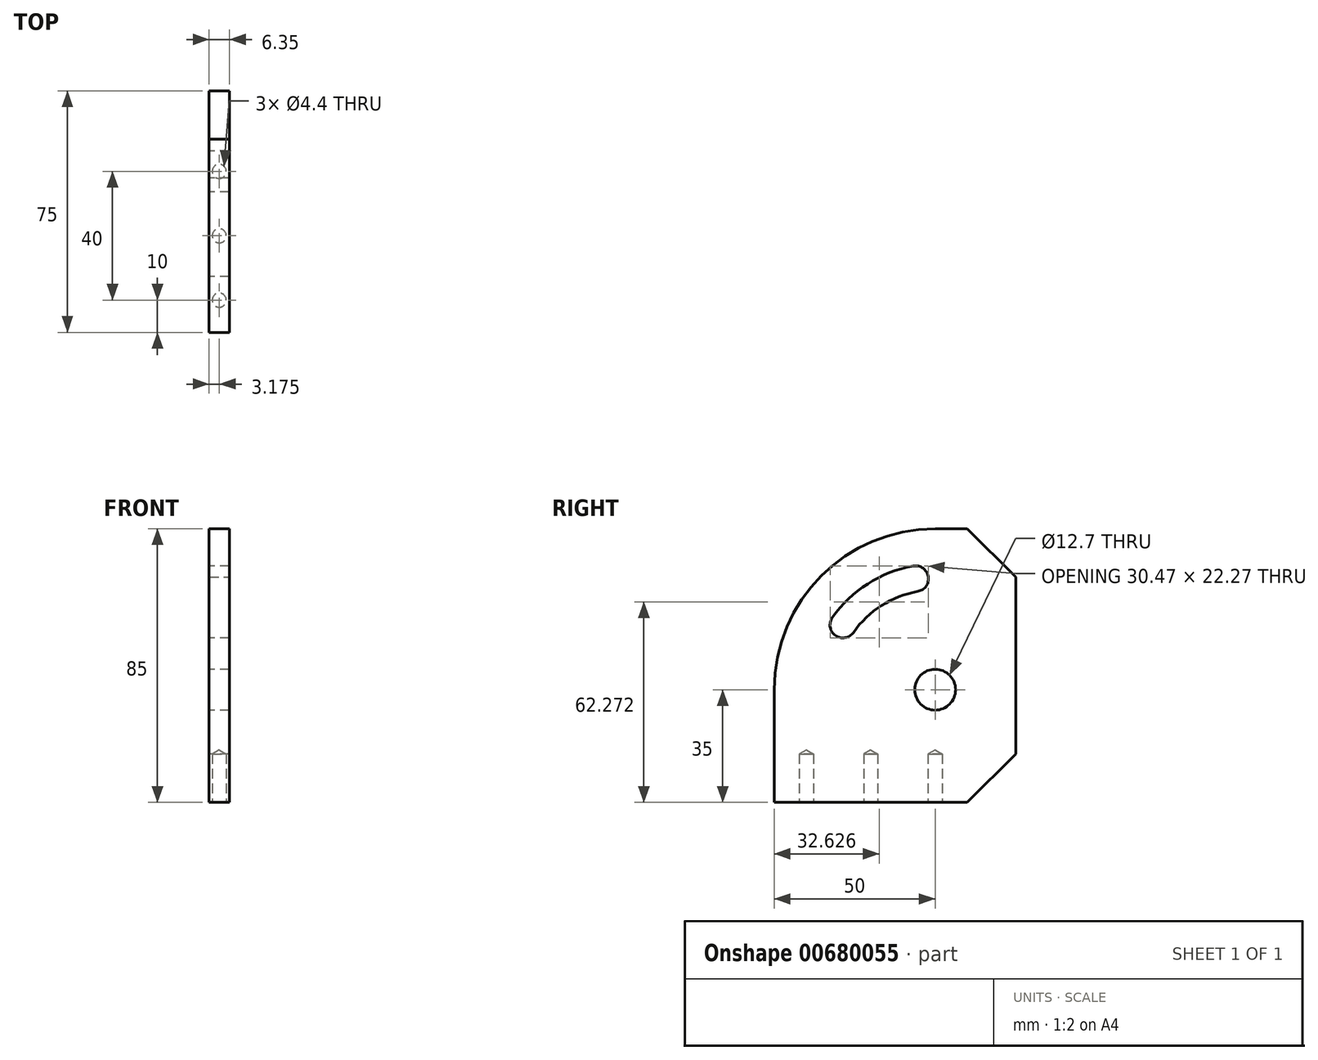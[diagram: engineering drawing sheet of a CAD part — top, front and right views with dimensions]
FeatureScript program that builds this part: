
annotation { "Feature Type Name" : "Feature", "Feature Type Description" : "" }
export const myFeature = defineFeature(function(context is Context, id is Id, definition is map)
    precondition{}
    {
        {
            var Q0;
            Q0=qCreatedBy(makeId("Right.planeOp"),FACE);
            var sketch = newSketch(context, id + "F0", { "sketchPlane" : qUnion([Q0])});
            skLineSegment(sketch, "E0", {"start": v(0, 0) * mm, "end": v(-75, 0) * mm});
            skLineSegment(sketch, "E1", {"start": v(-75, 0) * mm, "end": v(-75, 35) * mm});
            skArc(sketch, "E2", {"start": v(-25, 85) * mm, "mid": v(-60.36, 70.36) * mm, "end": v(-75, 35) * mm});
            skLineSegment(sketch, "E3", {"start": v(-25, 85) * mm, "end": v(0, 85) * mm});
            skLineSegment(sketch, "E4", {"start": v(0, 85) * mm, "end": v(0, 0) * mm});
            skArc(sketch, "E5", {"start": v(-56.95, 57.37) * mm, "mid": v(-45.95, 67.9) * mm, "end": v(-31.77, 73.4) * mm});
            skArc(sketch, "E6.0", {"start": v(-53.67, 55.08) * mm, "mid": v(-43.8, 64.52) * mm, "end": v(-31.08, 69.47) * mm, "construction": true});
            skArc(sketch, "E7.0", {"start": v(-50.4, 52.78) * mm, "mid": v(-41.66, 61.15) * mm, "end": v(-30.38, 65.53) * mm});
            skArc(sketch, "E8", {"start": v(-31.77, 73.4) * mm, "mid": v(-27.14, 70.16) * mm, "end": v(-30.38, 65.53) * mm});
            skArc(sketch, "E9", {"start": v(-56.95, 57.37) * mm, "mid": v(-55.96, 51.8) * mm, "end": v(-50.4, 52.78) * mm});
            skCircle(sketch, "E10", {"center": v(-25, 35) * mm, "radius": 6.35 * mm});
            skLineSegment(sketch, "E11", {"start": v(-31.08, 69.47) * mm, "end": v(-25, 35) * mm, "construction": true});
            skLineSegment(sketch, "E12", {"start": v(-53.67, 55.08) * mm, "end": v(-25, 35) * mm, "construction": true});
            skSolve(sketch);
        }
        {
            var Q0;
            Q0 = qSketchRegion(id + "F0", true);
            extrude(context, id + "F1", {"entities" : qUnion([Q0]), "depth" : 6.35 * mm, "offsetDistance" : 25 * mm});
        }
        {
            var Q0;
            Q0=makeQuery(id+"F1.opExtrude","SWEPT_EDGE",EDGE,{"disambiguationData":[OSD([sQuery(id+"F0.wireOp",EDGE,"E3"),sQuery(id+"F0.wireOp",EDGE,"E4")])]});
            var Q1;
            Q1=makeQuery(id+"F1.opExtrude","SWEPT_EDGE",EDGE,{"disambiguationData":[OSD([sQuery(id+"F0.wireOp",EDGE,"E0"),sQuery(id+"F0.wireOp",EDGE,"E4")])]});
            chamfer(context, id + "F2", {"entities" : qUnion([Q0, Q1]), "width" : 15 * mm, "tangentPropagation" : true});
        }
        {
            var Q0;
            Q0=makeQuery(id+"F1.opExtrude","SWEPT_FACE",FACE,{"disambiguationData":[OSD([sQuery(id+"F0.wireOp",EDGE,"E0")])]});
            var sketch = newSketch(context, id + "F3", { "sketchPlane" : qUnion([Q0])});
            skPoint(sketch, "E13", {"position": v(3.18, 65) * mm});
            skPoint(sketch, "E14", {"position": v(3.18, 45) * mm});
            skPoint(sketch, "E15", {"position": v(3.18, 25) * mm});
            skLineSegment(sketch, "E16", {"start": v(3.18, 65) * mm, "end": v(3.18, 45) * mm, "construction": true});
            skLineSegment(sketch, "E17", {"start": v(3.18, 25) * mm, "end": v(3.18, 45) * mm, "construction": true});
            skLineSegment(sketch, "E18", {"start": v(3.18, 65) * mm, "end": v(3.18, 75) * mm, "construction": true});
            skSolve(sketch);
        }
        {
            var Q0;
            Q0=sQuery(id+"F3.wireOp",VERTEX,"E13");
            var Q1;
            Q1=sQuery(id+"F3.wireOp",VERTEX,"E14");
            var Q2;
            Q2=sQuery(id+"F3.wireOp",VERTEX,"E15");
            var Q3;
            Q3=makeQuery(id+"F1.opExtrude","SWEPT_BODY",BODY,{"disambiguationData":[OSD([sQuery(id+"F0.wireOp",EDGE,"E0"),sQuery(id+"F0.wireOp",EDGE,"E1"),sQuery(id+"F0.wireOp",EDGE,"E2"),sQuery(id+"F0.wireOp",EDGE,"E3"),sQuery(id+"F0.wireOp",EDGE,"E4"),sQuery(id+"F0.wireOp",EDGE,"E5"),sQuery(id+"F0.wireOp",EDGE,"E7.0"),sQuery(id+"F0.wireOp",EDGE,"E8"),sQuery(id+"F0.wireOp",EDGE,"E9"),sQuery(id+"F0.wireOp",EDGE,"E10")])]});
            hole(context, id + "F4", {"style" : HoleStyle.SIMPLE, "endStyle" : HoleEndStyle.BLIND, "standardTappedOrClearance" : lookupTablePath({ "standard" : "ISO", "fit" : "Normal", "size" : "M4", "type" : "Clearance" }), "standardBlindInLast" : lookupTablePath({ "fit" : "Standard", "standard" : "ISO", "size" : "M4", "type" : "Clearance" }), "holeDiameter" : 4.4 * mm, "majorDiameter" : 5 * mm, "holeDepth" : 15 * mm, "isTappedThrough" : true, "tappedDepth" : 12 * mm, "tapClearance" : 3, "locations" : qUnion([Q0, Q1, Q2]), "scope" : qUnion([Q3])});
        }
    });
